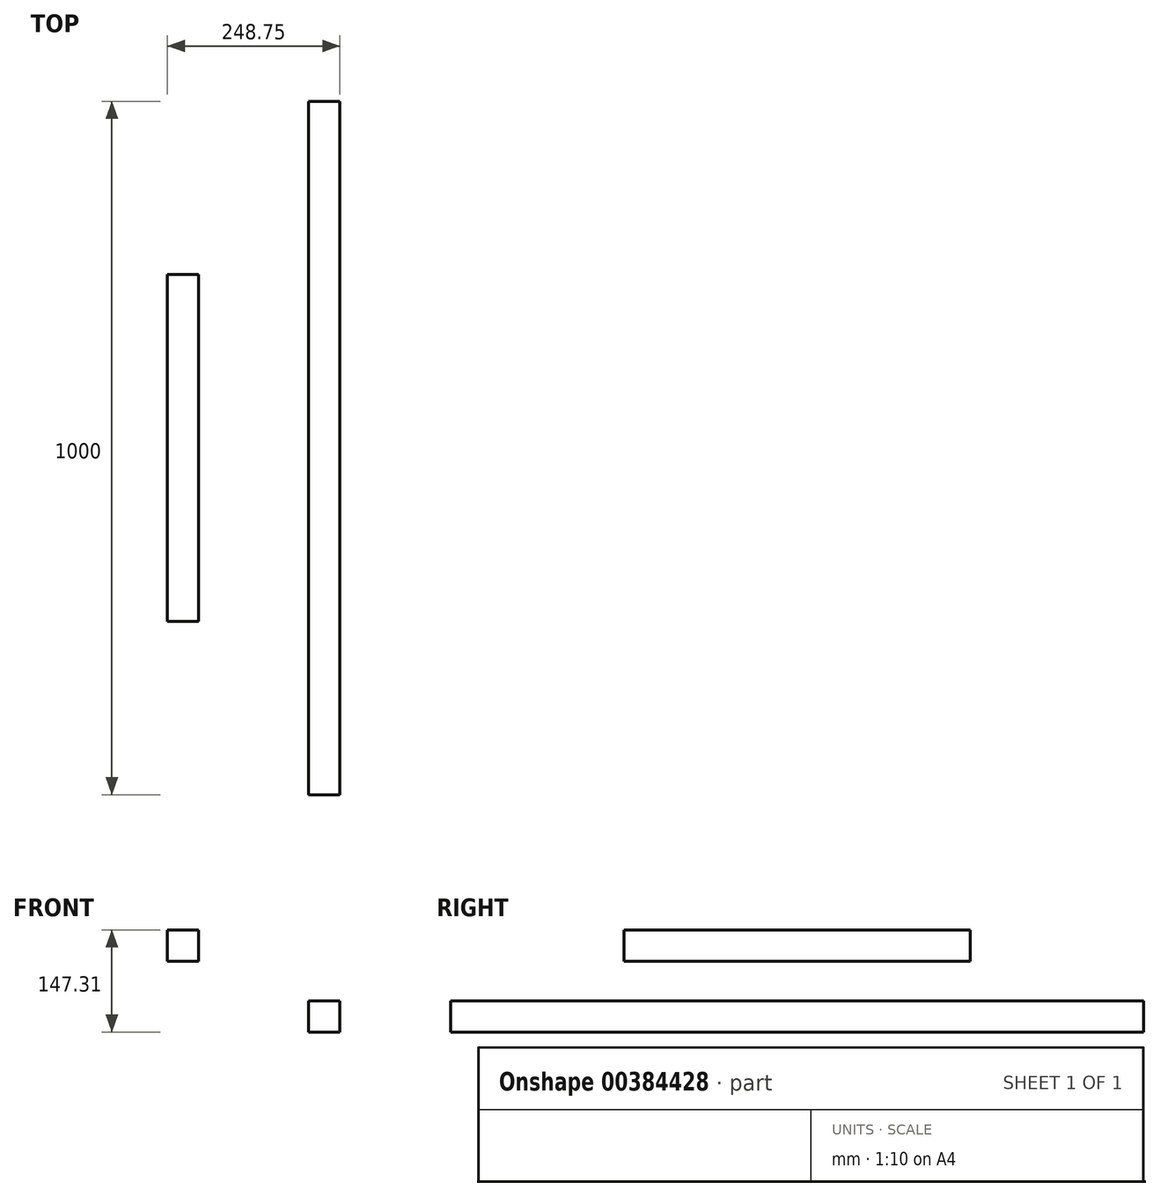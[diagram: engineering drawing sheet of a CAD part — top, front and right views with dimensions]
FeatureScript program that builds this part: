
annotation { "Feature Type Name" : "Feature", "Feature Type Description" : "" }
export const myFeature = defineFeature(function(context is Context, id is Id, definition is map)
    precondition{}
    {
        {
            var Q0;
            Q0=qCreatedBy(makeId("Front.planeOp"),FACE);
            var sketch = newSketch(context, id + "F0", { "sketchPlane" : qUnion([Q0])});
            skLineSegment(sketch, "E0.bottom", {"start": v(22.5, 22.5) * mm, "end": v(-22.5, 22.5) * mm});
            skLineSegment(sketch, "E0.top", {"start": v(22.5, -22.5) * mm, "end": v(-22.5, -22.5) * mm});
            skLineSegment(sketch, "E0.left", {"start": v(22.5, 22.5) * mm, "end": v(22.5, -22.5) * mm});
            skLineSegment(sketch, "E0.right", {"start": v(-22.5, 22.5) * mm, "end": v(-22.5, -22.5) * mm});
            skPoint(sketch, "E0.middle", {"position": v(0, 0) * mm});
            skSolve(sketch);
        }
        {
            var Q0;
            Q0 = qSketchRegion(id + "F0", true);
            extrude(context, id + "F1", {"entities" : qUnion([Q0]), "endBound" : BoundingType.SYMMETRIC, "depth" : 1000 * mm});
        }
        {
            var Q0;
            Q0=qCreatedBy(makeId("Front.planeOp"),FACE);
            var sketch = newSketch(context, id + "F2", { "sketchPlane" : qUnion([Q0])});
            skLineSegment(sketch, "E1.bottom", {"start": v(-181.25, 79.8) * mm, "end": v(-226.25, 79.8) * mm});
            skLineSegment(sketch, "E1.top", {"start": v(-181.25, 124.8) * mm, "end": v(-226.25, 124.8) * mm});
            skLineSegment(sketch, "E1.left", {"start": v(-181.25, 79.8) * mm, "end": v(-181.25, 124.8) * mm});
            skLineSegment(sketch, "E1.right", {"start": v(-226.25, 79.8) * mm, "end": v(-226.25, 124.8) * mm});
            skPoint(sketch, "E1.middle", {"position": v(-203.75, 102.3) * mm});
            skSolve(sketch);
        }
        {
            var Q0;
            Q0=makeQuery(id+"F2.imprint","IMPRINT",FACE,{"disambiguationData":[TD([[makeQuery(id+"F2.imprint","IMPRINT",EDGE,{"derivedFrom":sQuery(id+"F2.wireOp",EDGE,"E1.bottom")}),-1.0]])]});
            extrude(context, id + "F3", {"entities" : qUnion([Q0]), "endBound" : BoundingType.SYMMETRIC, "depth" : 500 * mm});
        }
    });
